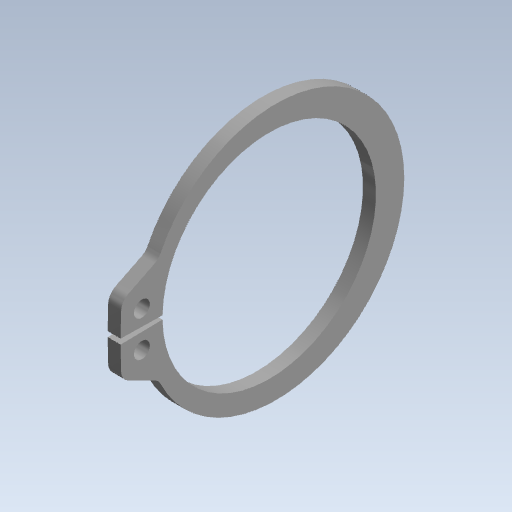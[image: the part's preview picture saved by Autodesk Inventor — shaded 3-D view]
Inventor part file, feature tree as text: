
AUTODESK INVENTOR PART (.ipt)
format: ipt  version: 2020 (Build 240168000, 168)  size: 86,016 bytes
history: native  units: mm (DEFAULTED — no unit token found)
features: fillet x1
ambient origin geometry x8: Origin, YZ Plane, XZ Plane, XY Plane, X Axis, Y Axis, Z Axis, Center Point
bodies: Solid1 (feature_tree)
feature tree (1):
  fillet  "Fillet1"  [1 undecoded]
note: 1 required parameter value undecoded (feature->parameter linkage not recoverable at this tier; creation-order binding heuristic only, values carry confidence <= 0.55)
